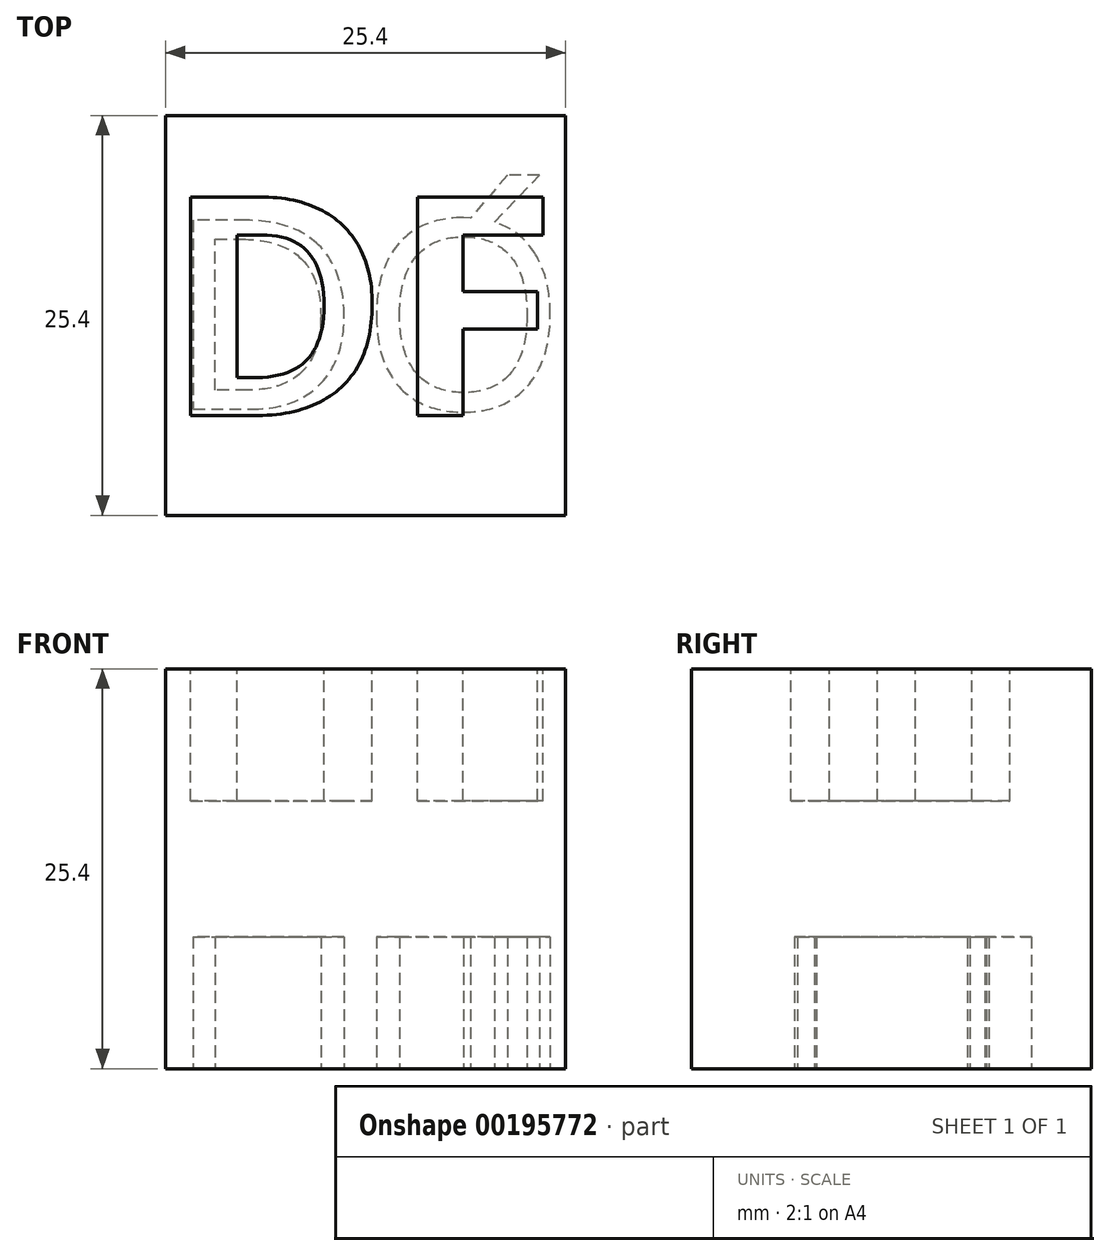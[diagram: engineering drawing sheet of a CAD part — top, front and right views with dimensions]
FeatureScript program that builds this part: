
annotation { "Feature Type Name" : "Feature", "Feature Type Description" : "" }
export const myFeature = defineFeature(function(context is Context, id is Id, definition is map)
    precondition{}
    {
        {
            var Q0;
            Q0=qCreatedBy(makeId("Top.planeOp"),FACE);
            var sketch = newSketch(context, id + "F0", { "sketchPlane" : qUnion([Q0])});
            skLineSegment(sketch, "E0.bottom", {"start": v(-13.6, 12.58) * mm, "end": v(11.8, 12.58) * mm});
            skLineSegment(sketch, "E0.top", {"start": v(-13.6, -12.82) * mm, "end": v(11.8, -12.82) * mm});
            skLineSegment(sketch, "E0.left", {"start": v(-13.6, 12.58) * mm, "end": v(-13.6, -12.82) * mm});
            skLineSegment(sketch, "E0.right", {"start": v(11.8, 12.58) * mm, "end": v(11.8, -12.82) * mm});
            skSolve(sketch);
        }
        {
            var Q0;
            Q0 = qSketchRegion(id + "F0", true);
            extrude(context, id + "F1", {"entities" : qUnion([Q0]), "depth" : 25.4 * mm});
        }
        {
            var Q0;
            Q0=makeQuery(id+"F1.opExtrude","CAP_FACE",FACE,{"disambiguationData":[OSD([sQuery(id+"F0.wireOp",EDGE,"E0.bottom"),sQuery(id+"F0.wireOp",EDGE,"E0.top"),sQuery(id+"F0.wireOp",EDGE,"E0.left"),sQuery(id+"F0.wireOp",EDGE,"E0.right")])],"isStart":false});
            var sketch = newSketch(context, id + "F2", { "sketchPlane" : qUnion([Q0])});
            skText(sketch, "E1", { "text": "DF", "fontName": "OpenSans-Bold.ttf"});
            const initialGuessF2  = {"E1": [-0.01377, -0.0065, 1, 0, 0.01402]};
            skSetInitialGuess(sketch, initialGuessF2);
            skSolve(sketch);
        }
        {
            var Q0;
            Q0 = qSketchRegion(id + "F2", true);
            extrude(context, id + "F3", {"entities" : qUnion([Q0]), "operationType" : NewBodyOperationType.REMOVE, "oppositeDirection" : true, "depth" : 8.38 * mm});
        }
        {
            var Q0;
            Q0=makeQuery(id+"F1.opExtrude","CAP_FACE",FACE,{"disambiguationData":[OSD([sQuery(id+"F0.wireOp",EDGE,"E0.bottom"),sQuery(id+"F0.wireOp",EDGE,"E0.top"),sQuery(id+"F0.wireOp",EDGE,"E0.left"),sQuery(id+"F0.wireOp",EDGE,"E0.right")])],"isStart":true});
            var sketch = newSketch(context, id + "F4", { "sketchPlane" : qUnion([Q0])});
            skText(sketch, "E2", { "text": "DQ", "fontName": "OpenSans-Regular.ttf"});
            const initialGuessF4  = {"E2": [-0.0135, -0.00592, 1, 0, 0.0121]};
            skSetInitialGuess(sketch, initialGuessF4);
            skSolve(sketch);
        }
        {
            var Q0;
            Q0 = qSketchRegion(id + "F4", true);
            extrude(context, id + "F5", {"entities" : qUnion([Q0]), "operationType" : NewBodyOperationType.REMOVE, "oppositeDirection" : true, "depth" : 8.38 * mm});
        }
    });
